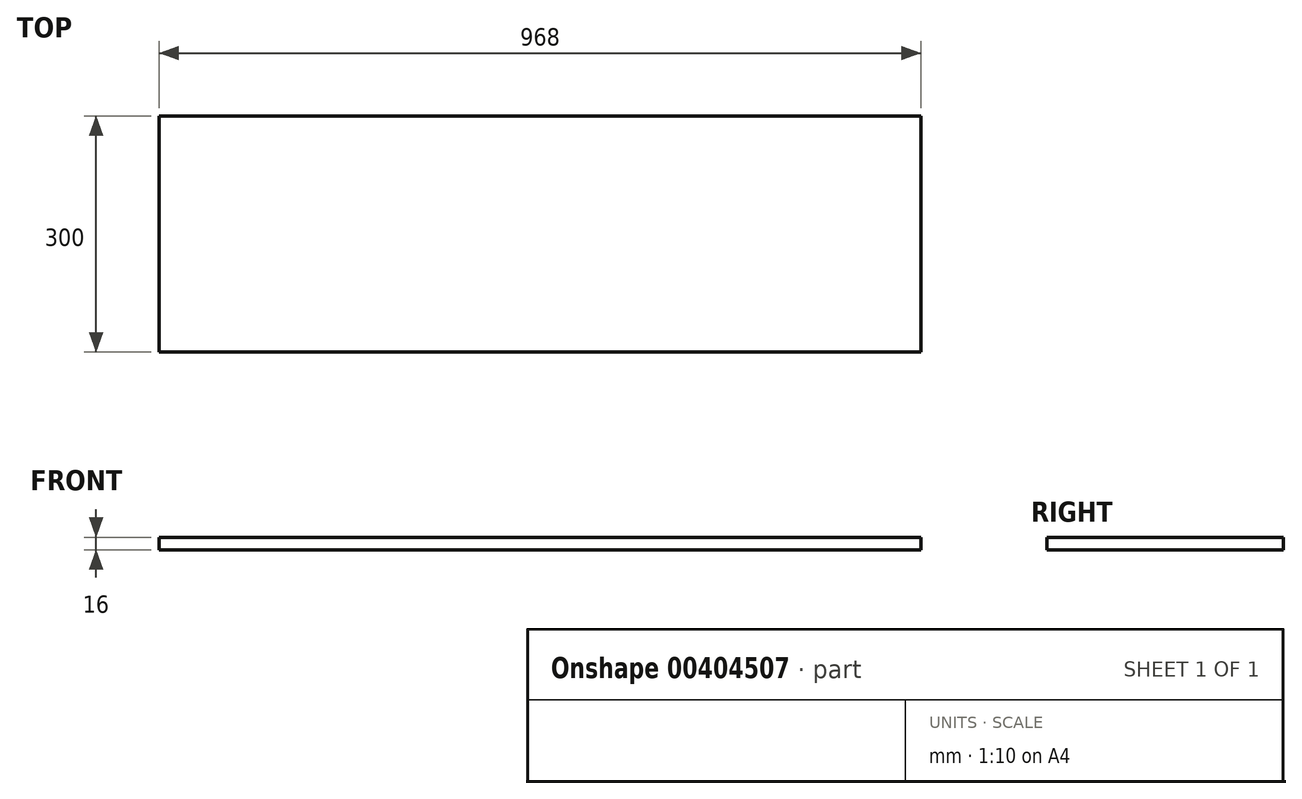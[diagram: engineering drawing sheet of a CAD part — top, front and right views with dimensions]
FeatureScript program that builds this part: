
annotation { "Feature Type Name" : "Feature", "Feature Type Description" : "" }
export const myFeature = defineFeature(function(context is Context, id is Id, definition is map)
    precondition{}
    {
        {
            var Q0;
            Q0=qCreatedBy(makeId("Top.planeOp"),FACE);
            var sketch = newSketch(context, id + "F0", { "sketchPlane" : qUnion([Q0])});
            skLineSegment(sketch, "E0.bottom", {"start": v(0, 0) * mm, "end": v(57.74, 0) * mm});
            skLineSegment(sketch, "E0.top", {"start": v(0, -53.4) * mm, "end": v(57.74, -53.4) * mm});
            skLineSegment(sketch, "E0.left", {"start": v(0, 0) * mm, "end": v(0, -53.4) * mm});
            skLineSegment(sketch, "E0.right", {"start": v(57.74, 0) * mm, "end": v(57.74, -53.4) * mm});
            skSolve(sketch);
        }
        {
            var Q0;
            Q0=makeQuery(id+"F0.imprint","IMPRINT",FACE,{"disambiguationData":[TD([[makeQuery(id+"F0.imprint","IMPRINT",EDGE,{"derivedFrom":sQuery(id+"F0.wireOp",EDGE,"E0.bottom")}),-1.0]])]});
            extrude(context, id + "F1", {"entities" : qUnion([Q0]), "depth" : 16 * mm});
        }
        {
            var Q0;
            Q0=makeQuery(id+"F1.opExtrude","SWEPT_FACE",FACE,{"disambiguationData":[OSD([sQuery(id+"F0.wireOp",EDGE,"E0.left")])]});
            extrude(context, id + "F2", {"entities" : qUnion([Q0]), "operationType" : NewBodyOperationType.ADD, "oppositeDirection" : true, "depth" : 968 * mm});
        }
        {
            var Q0;
            {var subQ0=sQuery(id+"F0.wireOp",EDGE,"E0.bottom");Q0=makeQuery(id+"F2.boolean.opBoolean","MERGE",FACE,{"derivedFrom":[makeQuery(id+"F1.opExtrude","SWEPT_FACE",FACE,{"disambiguationData":[OSD([subQ0])]}),makeQuery(id+"F2.opExtrude","SWEPT_FACE",FACE,{"disambiguationData":[OSD([subQ0,sQuery(id+"F0.wireOp",EDGE,"E0.left")])]})]});}
            extrude(context, id + "F3", {"entities" : qUnion([Q0]), "operationType" : NewBodyOperationType.ADD, "oppositeDirection" : true, "depth" : 300 * mm});
        }
    });
